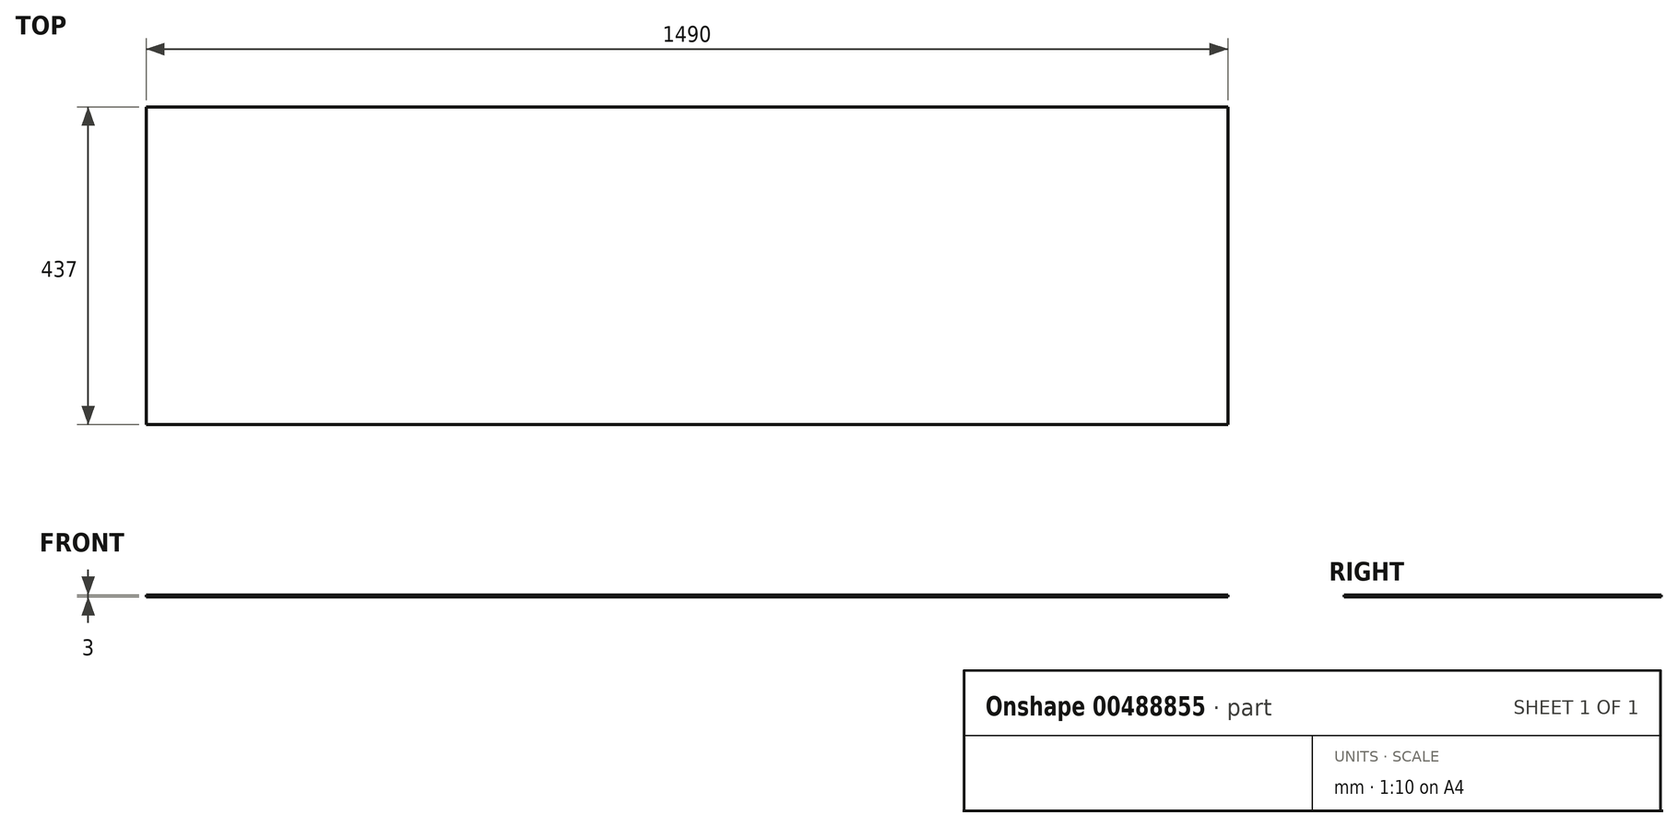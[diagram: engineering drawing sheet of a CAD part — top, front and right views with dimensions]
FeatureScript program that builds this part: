
annotation { "Feature Type Name" : "Feature", "Feature Type Description" : "" }
export const myFeature = defineFeature(function(context is Context, id is Id, definition is map)
    precondition{}
    {
        {
            var Q0;
            Q0=qCreatedBy(makeId("Top.planeOp"),FACE);
            var sketch = newSketch(context, id + "F0", { "sketchPlane" : qUnion([Q0])});
            skLineSegment(sketch, "E0.bottom", {"start": v(-755.66, 172.25) * mm, "end": v(734.34, 172.25) * mm});
            skLineSegment(sketch, "E0.top", {"start": v(-755.66, -264.75) * mm, "end": v(734.34, -264.75) * mm});
            skLineSegment(sketch, "E0.left", {"start": v(-755.66, 172.25) * mm, "end": v(-755.66, -264.75) * mm});
            skLineSegment(sketch, "E0.right", {"start": v(734.34, 172.25) * mm, "end": v(734.34, -264.75) * mm});
            skSolve(sketch);
        }
        {
            var Q0;
            Q0=makeQuery(id+"F0.imprint","IMPRINT",FACE,{"disambiguationData":[TD([[makeQuery(id+"F0.imprint","IMPRINT",EDGE,{"derivedFrom":sQuery(id+"F0.wireOp",EDGE,"E0.bottom")}),-1.0]])]});
            extrude(context, id + "F1", {"entities" : qUnion([Q0]), "depth" : 3 * mm});
        }
    });
